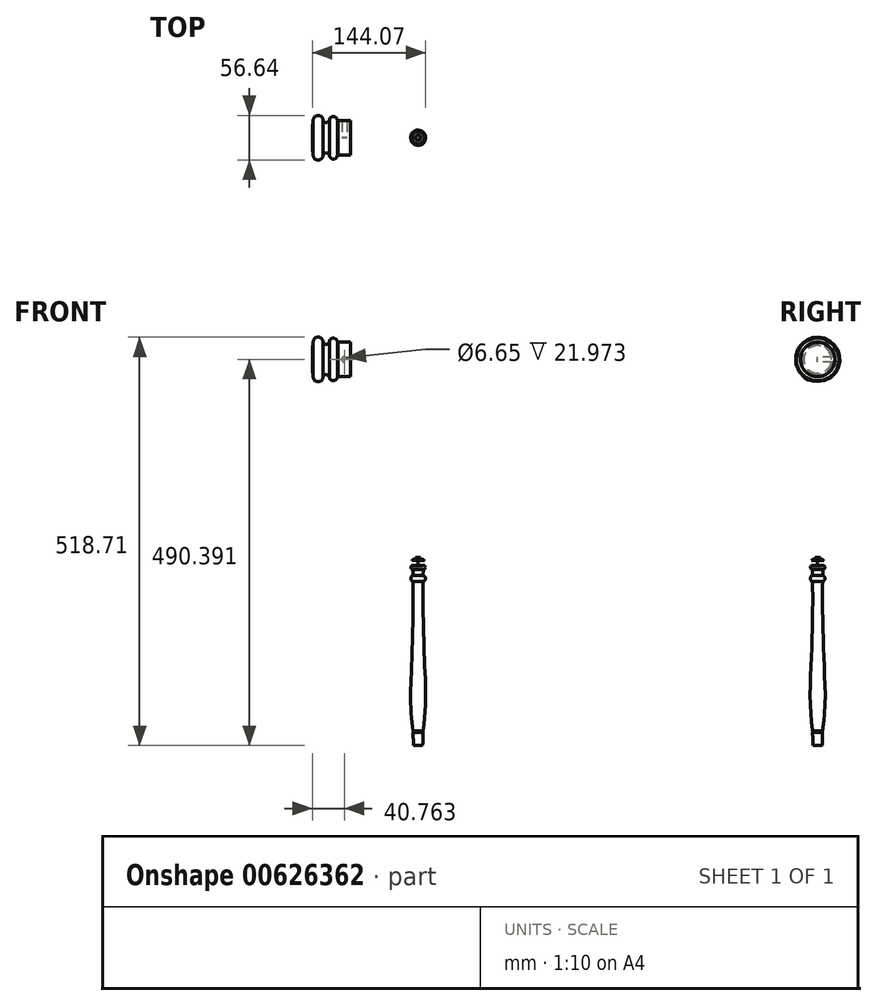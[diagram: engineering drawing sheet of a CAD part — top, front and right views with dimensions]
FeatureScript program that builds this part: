
annotation { "Feature Type Name" : "Feature", "Feature Type Description" : "" }
export const myFeature = defineFeature(function(context is Context, id is Id, definition is map)
    precondition{}
    {
        {
            var Q0;
            Q0=qCreatedBy(makeId("Front.planeOp"),FACE);
            var sketch = newSketch(context, id + "F0", { "sketchPlane" : qUnion([Q0])});
            skPoint(sketch, "E0.endSnap0", {"position": v(-10.43, 232.28) * mm});
            skLineSegment(sketch, "E1", {"start": v(-4.53, 234.95) * mm, "end": v(-9.23, 234.95) * mm});
            skArc(sketch, "E2", {"start": v(-42, 240.44) * mm, "mid": v(-41.7, 239.72) * mm, "end": v(-40.98, 239.43) * mm});
            skLineSegment(sketch, "E3.trimOffspring", {"start": v(-40.98, 239.43) * mm, "end": v(-40.98, 234.95) * mm});
            skArc(sketch, "E4.MirrorCS", {"start": v(39.54, 240.44) * mm, "mid": v(39.24, 239.72) * mm, "end": v(38.52, 239.43) * mm});
            skLineSegment(sketch, "E5.MirrorCS", {"start": v(38.52, 239.43) * mm, "end": v(38.52, 234.95) * mm});
            skLineSegment(sketch, "E6.MirrorCS", {"start": v(6.77, 234.95) * mm, "end": v(7.79, 234.95) * mm});
            skLineSegment(sketch, "E7.MirrorCS", {"start": v(-1.23, 234.95) * mm, "end": v(6.77, 234.95) * mm});
            skPoint(sketch, "E8.startSnap0", {"position": v(-19.7, 256.92) * mm});
            skArc(sketch, "E9", {"start": v(-40.98, 234.95) * mm, "mid": v(-34.63, 228.6) * mm, "end": v(-28.28, 234.95) * mm});
            skArc(sketch, "E10.MirrorCS", {"start": v(38.52, 234.95) * mm, "mid": v(32.17, 228.6) * mm, "end": v(25.82, 234.95) * mm});
            skLineSegment(sketch, "E11", {"start": v(39.54, 256.92) * mm, "end": v(-42, 256.92) * mm});
            skLineSegment(sketch, "E12", {"start": v(39.54, 256.92) * mm, "end": v(39.54, 240.44) * mm});
            skLineSegment(sketch, "E13", {"start": v(-42, 240.44) * mm, "end": v(-42, 256.92) * mm});
            skLineSegment(sketch, "E14", {"start": v(-22.66, 234.95) * mm, "end": v(-20.4, 234.95) * mm});
            skArc(sketch, "E15", {"start": v(-20.4, 234.95) * mm, "mid": v(-15.32, 229.87) * mm, "end": v(-10.24, 234.95) * mm});
            skFitSpline(sketch, "E16", {"points": [v(-28.28, 234.95) * mm, v(-24.6, 237.8) * mm, v(-20.4, 234.95) * mm], "startDerivative": vector(7.34, 8.63) * mm, "endDerivative": vector(8.4, -8.5) * mm});
            skLineSegment(sketch, "E17.trimOffspring", {"start": v(-10.24, 234.95) * mm, "end": v(-9.23, 234.95) * mm});
            skArc(sketch, "E18.MirrorCS", {"start": v(17.95, 234.95) * mm, "mid": v(12.87, 229.87) * mm, "end": v(7.79, 234.95) * mm});
            skFitSpline(sketch, "E19.MirrorCS", {"points": [v(25.82, 234.95) * mm, v(22.15, 237.8) * mm, v(17.95, 234.95) * mm], "startDerivative": vector(-7.34, 8.63) * mm, "endDerivative": vector(-8.4, -8.5) * mm});
            skLineSegment(sketch, "E20", {"start": v(-9.23, 234.95) * mm, "end": v(-9.23, 256.92) * mm});
            skLineSegment(sketch, "E21", {"start": v(6.77, 234.95) * mm, "end": v(6.77, 256.92) * mm});
            skLineSegment(sketch, "E22", {"start": v(86.7, -216.96) * mm, "end": v(86.13, -216.96) * mm});
            skFitSpline(sketch, "E23", {"points": [v(86.13, -216.96) * mm, v(86.7, -233.47) * mm], "startDerivative": vector(-0.01, -17.53) * mm, "endDerivative": vector(1.46, -15.8) * mm});
            skArc(sketch, "E24", {"start": v(86.13, -216.96) * mm, "mid": v(86.36, -216) * mm, "end": v(86.13, -215.05) * mm});
            skLineSegment(sketch, "E25", {"start": v(86.7, -233.47) * mm, "end": v(92.42, -233.47) * mm});
            skLineSegment(sketch, "E26", {"start": v(92.42, -233.47) * mm, "end": v(92.42, -25.19) * mm});
            skLineSegment(sketch, "E27", {"start": v(92.42, -25.19) * mm, "end": v(92.42, -17.31) * mm});
            skFitSpline(sketch, "E28", {"points": [v(86.13, -215.05) * mm, v(82.95, -179.9) * mm, v(83.88, -137.4) * mm, v(85.94, -25.19) * mm], "startDerivative": vector(-15, 108.64) * mm, "endDerivative": vector(-5.7, 193.06) * mm});
            skArc(sketch, "E29", {"start": v(85.94, -17.31) * mm, "mid": v(83.15, -21.25) * mm, "end": v(85.94, -25.19) * mm});
            skPoint(sketch, "E30.orphan", {"position": v(92.42, -21.25) * mm});
            skPoint(sketch, "E31.endSnap0", {"position": v(83.21, -1.18) * mm});
            skArc(sketch, "E32", {"start": v(84.42, -4.87) * mm, "mid": v(83.37, -7.42) * mm, "end": v(84.67, -9.86) * mm});
            skArc(sketch, "E33", {"start": v(84.42, 1.48) * mm, "mid": v(83.19, -1.7) * mm, "end": v(84.42, -4.87) * mm});
            skLineSegment(sketch, "E34", {"start": v(84.67, -9.86) * mm, "end": v(85.68, -9.86) * mm});
            skLineSegment(sketch, "E35", {"start": v(85.68, -9.86) * mm, "end": v(85.94, -17.31) * mm});
            skLineSegment(sketch, "E36", {"start": v(92.42, 1.48) * mm, "end": v(92.42, -17.31) * mm});
            skLineSegment(sketch, "E37", {"start": v(89.12, 1.48) * mm, "end": v(84.42, 1.48) * mm});
            skLineSegment(sketch, "E38", {"start": v(92.42, 5.42) * mm, "end": v(89.12, 5.42) * mm});
            skLineSegment(sketch, "E39", {"start": v(89.12, 5.42) * mm, "end": v(89.12, 1.48) * mm});
            skLineSegment(sketch, "E40", {"start": v(92.42, 1.48) * mm, "end": v(92.42, 5.42) * mm});
            skLineSegment(sketch, "E41", {"start": v(-1.23, 234.95) * mm, "end": v(-4.53, 234.95) * mm});
            skPoint(sketch, "E42", {"position": v(-1.23, 245.94) * mm});
            skPoint(sketch, "E43.orphan", {"position": v(-1.23, 256.92) * mm});
            skPoint(sketch, "E44.orphan", {"position": v(6.77, 245.94) * mm});
            skPoint(sketch, "E45.start.orphan", {"position": v(-9.23, 245.94) * mm});
            skSolve(sketch);
        }
        {
            var Q0;
            Q0=makeQuery(id+"F0.imprint","IMPRINT",FACE,{"disambiguationData":[TD([[makeQuery(id+"F0.imprint","IMPRINT",EDGE,{"derivedFrom":sQuery(id+"F0.wireOp",EDGE,"E2")}),1.0]])]});
            var Q1;
            Q1=makeQuery(id+"F0.imprint","IMPRINT",FACE,{"disambiguationData":[TD([[makeQuery(id+"F0.imprint","IMPRINT",EDGE,{"derivedFrom":sQuery(id+"F0.wireOp",EDGE,"E4.MirrorCS")}),-1.0]])]});
            var Q2;
            Q2=sQuery(id+"F0.wireOp",EDGE,"E11");
            revolve(context, id + "F1", {"entities" : qUnion([Q0, Q1]), "axis" : qUnion([Q2]), "revolveType" : RevolveType.FULL});
        }
        {
            var Q0;
            {var subQ1=sQuery(id+"F0.wireOp",EDGE,"E2");Q0=makeQuery(id+"F0.imprint","IMPRINT",FACE,{"disambiguationData":[TD([[makeQuery(id+"F0.imprint","IMPRINT",EDGE,{"derivedFrom":subQ1}),1.0]])]});}
            var Q1;
            Q1=makeQuery(id+"F0.imprint","IMPRINT",FACE,{"disambiguationData":[TD([[makeQuery(id+"F0.imprint","IMPRINT",EDGE,{"derivedFrom":sQuery(id+"F0.wireOp",EDGE,"E4.MirrorCS")}),-1.0]])]});
            var Q2;
            Q2=sQuery(id+"F0.wireOp",EDGE,"E11");
            revolve(context, id + "F2", {"operationType" : NewBodyOperationType.ADD, "entities" : qUnion([Q0, Q1]), "axis" : qUnion([Q2]), "revolveType" : RevolveType.FULL});
        }
        {
            var Q0;
            Q0=makeQuery(id+"F0.imprint","IMPRINT",FACE,{"disambiguationData":[TD([[makeQuery(id+"F0.imprint","IMPRINT",EDGE,{"derivedFrom":sQuery(id+"F0.wireOp",EDGE,"E1")}),-1.0]])]});
            var Q1;
            Q1=sQuery(id+"F0.wireOp",EDGE,"E11");
            revolve(context, id + "F3", {"entities" : qUnion([Q0]), "axis" : qUnion([Q1]), "revolveType" : RevolveType.FULL});
        }
        {
            var Q0;
            Q0=makeQuery(id+"F0.imprint","IMPRINT",FACE,{"disambiguationData":[TD([[makeQuery(id+"F0.imprint","IMPRINT",EDGE,{"derivedFrom":sQuery(id+"F0.wireOp",EDGE,"E23")}),1.0]])]});
            var Q1;
            Q1=sQuery(id+"F0.wireOp",EDGE,"E26");
            revolve(context, id + "F4", {"entities" : qUnion([Q0]), "axis" : qUnion([Q1]), "revolveType" : RevolveType.FULL});
        }
        {
            var Q0;
            Q0=sQuery(id+"F0.wireOp",VERTEX,"E43.orphan");
            var Q1;
            Q1=makeQuery(id+"F3.opRevolve","SWEPT_BODY",BODY,{"disambiguationData":[OSD([sQuery(id+"F0.wireOp",EDGE,"E1"),sQuery(id+"F0.wireOp",EDGE,"E7.MirrorCS"),sQuery(id+"F0.wireOp",EDGE,"E11"),sQuery(id+"F0.wireOp",EDGE,"E20"),sQuery(id+"F0.wireOp",EDGE,"E21"),sQuery(id+"F0.wireOp",EDGE,"E41")])]});
            hole(context, id + "F5", {"style" : HoleStyle.SIMPLE, "endStyle" : HoleEndStyle.THROUGH, "holeDiameter" : 6.65 * mm, "majorDiameter" : 6.35 * mm, "isTappedThrough" : true, "tappedDepth" : 12.7 * mm, "tapClearance" : 3, "locations" : qUnion([Q0]), "scope" : qUnion([Q1])});
        }
    });
